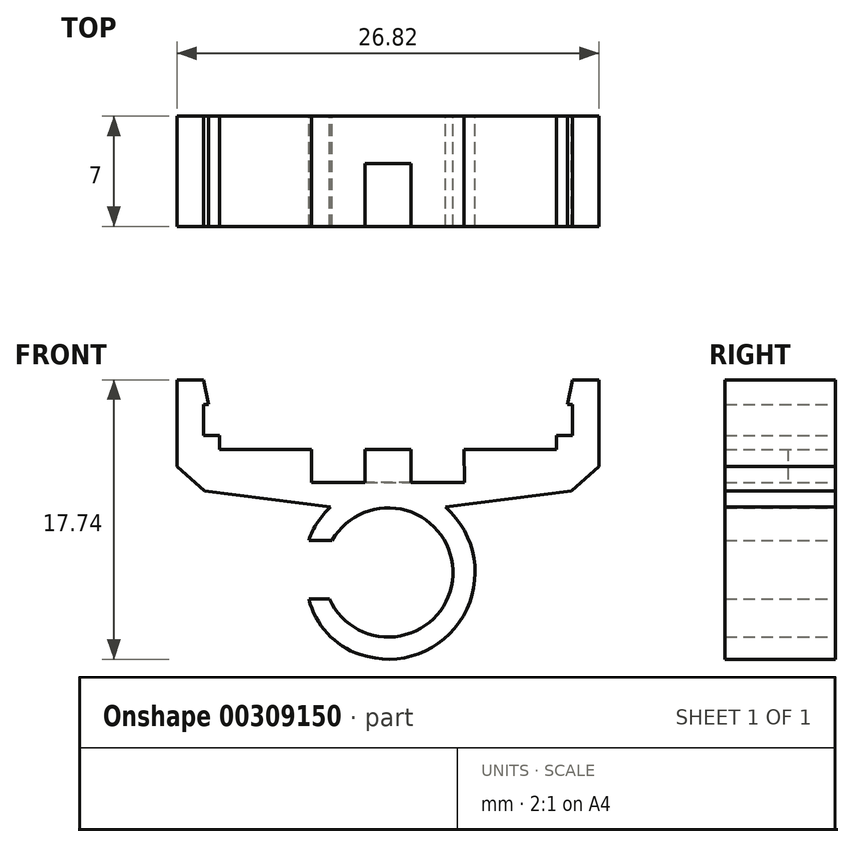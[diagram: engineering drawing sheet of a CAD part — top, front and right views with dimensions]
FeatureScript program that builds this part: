
annotation { "Feature Type Name" : "Feature", "Feature Type Description" : "" }
export const myFeature = defineFeature(function(context is Context, id is Id, definition is map)
    precondition{}
    {
        {
            var Q0;
            Q0=qCreatedBy(makeId("Front.planeOp"),FACE);
            var sketch = newSketch(context, id + "F0", { "sketchPlane" : qUnion([Q0])});
            skLineSegment(sketch, "E0", {"start": v(-2.98, 4.62) * mm, "end": v(-2.98, 4.65) * mm});
            skArc(sketch, "E1.trimOffspring", {"start": v(-1.78, -5.2) * mm, "mid": v(4.78, -2.76) * mm, "end": v(3.65, 4.15) * mm});
            skArc(sketch, "E2", {"start": v(-3.65, 4.15) * mm, "mid": v(-4.48, 3.19) * mm, "end": v(-5.03, 2.04) * mm});
            skArc(sketch, "E3", {"start": v(-5.03, -1.68) * mm, "mid": v(-3.86, -3.86) * mm, "end": v(-1.78, -5.2) * mm});
            skLineSegment(sketch, "E4", {"start": v(11.65, 5.17) * mm, "end": v(13.41, 6.73) * mm});
            skLineSegment(sketch, "E5", {"start": v(11.7, 8.7) * mm, "end": v(11.7, 9.57) * mm});
            skLineSegment(sketch, "E6", {"start": v(11.7, 12.23) * mm, "end": v(13.41, 12.23) * mm});
            skLineSegment(sketch, "E7", {"start": v(13.41, 6.73) * mm, "end": v(13.41, 12.23) * mm});
            skLineSegment(sketch, "E8.MirrorCS", {"start": v(-11.65, 5.17) * mm, "end": v(-13.41, 6.73) * mm});
            skLineSegment(sketch, "E9.MirrorCS", {"start": v(-13.41, 6.73) * mm, "end": v(-13.41, 12.23) * mm});
            skLineSegment(sketch, "E10.MirrorCS", {"start": v(-11.7, 8.7) * mm, "end": v(-11.7, 9.57) * mm});
            skLineSegment(sketch, "E11.MirrorCS", {"start": v(-11.7, 12.23) * mm, "end": v(-13.41, 12.23) * mm});
            skLineSegment(sketch, "E12", {"start": v(3.65, 4.15) * mm, "end": v(11.65, 5.17) * mm});
            skLineSegment(sketch, "E13.MirrorCS", {"start": v(-3.65, 4.15) * mm, "end": v(-11.65, 5.17) * mm});
            skPoint(sketch, "E14.MirrorCS.end.orphan", {"position": v(-11.65, 5.17) * mm});
            skLineSegment(sketch, "E15", {"start": v(-4.86, 5.72) * mm, "end": v(4.86, 5.72) * mm});
            skLineSegment(sketch, "E16", {"start": v(-10.7, 7.82) * mm, "end": v(-4.86, 7.82) * mm});
            skLineSegment(sketch, "E17", {"start": v(4.84, 7.82) * mm, "end": v(10.7, 7.82) * mm});
            skLineSegment(sketch, "E18", {"start": v(-4.86, 5.72) * mm, "end": v(-4.86, 7.82) * mm});
            skLineSegment(sketch, "E19", {"start": v(4.86, 5.72) * mm, "end": v(4.84, 7.82) * mm});
            skLineSegment(sketch, "E20", {"start": v(11.7, 8.7) * mm, "end": v(11.7, 10.66) * mm});
            skLineSegment(sketch, "E21", {"start": v(11.7, 8.7) * mm, "end": v(10.7, 8.7) * mm});
            skLineSegment(sketch, "E22", {"start": v(10.7, 8.7) * mm, "end": v(10.7, 7.82) * mm});
            skPoint(sketch, "E23.orphan", {"position": v(11.7, 7.82) * mm});
            skLineSegment(sketch, "E24.MirrorCS", {"start": v(-10.7, 8.7) * mm, "end": v(-10.7, 7.82) * mm});
            skLineSegment(sketch, "E25.MirrorCS", {"start": v(-11.7, 8.7) * mm, "end": v(-10.7, 8.7) * mm});
            skLineSegment(sketch, "E26.MirrorCS", {"start": v(-11.7, 8.7) * mm, "end": v(-11.7, 10.66) * mm});
            skPoint(sketch, "E27.orphan", {"position": v(-11.7, 9.57) * mm});
            skPoint(sketch, "E28.orphan", {"position": v(-11.7, 7.82) * mm});
            skLineSegment(sketch, "E29", {"start": v(-11.7, 10.66) * mm, "end": v(-11.7, 12.23) * mm});
            skLineSegment(sketch, "E30", {"start": v(11.7, 10.66) * mm, "end": v(11.7, 12.23) * mm});
            skPoint(sketch, "E31.MirrorCS.start.orphan", {"position": v(-11.7, 10.66) * mm});
            skLineSegment(sketch, "E32", {"start": v(-11.7, 10.66) * mm, "end": v(-11.4, 10.66) * mm});
            skLineSegment(sketch, "E33", {"start": v(-11.4, 10.66) * mm, "end": v(-11.7, 12.23) * mm});
            skLineSegment(sketch, "E34", {"start": v(11.7, 10.66) * mm, "end": v(11.4, 10.66) * mm});
            skLineSegment(sketch, "E35", {"start": v(11.4, 10.66) * mm, "end": v(11.7, 12.23) * mm});
            skLineSegment(sketch, "E36", {"start": v(0, 5.72) * mm, "end": v(0, 7.82) * mm, "construction": true});
            skLineSegment(sketch, "E37", {"start": v(0, 7.82) * mm, "end": v(-1.45, 7.82) * mm});
            skLineSegment(sketch, "E38.MirrorCS", {"start": v(0, 7.82) * mm, "end": v(1.45, 7.82) * mm});
            skLineSegment(sketch, "E39", {"start": v(-1.45, 7.82) * mm, "end": v(-1.45, 5.72) * mm});
            skLineSegment(sketch, "E40", {"start": v(1.45, 7.82) * mm, "end": v(1.45, 5.72) * mm});
            skArc(sketch, "E41", {"start": v(-3.73, -1.68) * mm, "mid": v(4.12, -0.2) * mm, "end": v(-3.55, 2.04) * mm});
            skLineSegment(sketch, "E42", {"start": v(-5.03, 2.04) * mm, "end": v(-3.55, 2.04) * mm});
            skLineSegment(sketch, "E43", {"start": v(-5.03, -1.68) * mm, "end": v(-3.73, -1.68) * mm});
            skLineSegment(sketch, "E44", {"start": v(-4.81, -2.36) * mm, "end": v(5, 2.35) * mm, "construction": true});
            skLineSegment(sketch, "E45", {"start": v(-3.05, 2.73) * mm, "end": v(3.11, -2.7) * mm, "construction": true});
            skSolve(sketch);
        }
        {
            var Q0;
            Q0 = qSketchRegion(id + "F0", true);
            extrude(context, id + "F1", {"entities" : qUnion([Q0]), "depth" : 7 * mm});
        }
        {
            var Q0;
            Q0=makeQuery(id+"F1.opExtrude","CAP_FACE",FACE,{"disambiguationData":[OSD([sQuery(id+"F0.wireOp",EDGE,"E1.trimOffspring"),sQuery(id+"F0.wireOp",EDGE,"E2"),sQuery(id+"F0.wireOp",EDGE,"E3"),sQuery(id+"F0.wireOp",EDGE,"znFwvZoN-sigT-Xg2n-eal0-1niIN2wFVg9l"),sQuery(id+"F0.wireOp",EDGE,"9Rdlhenn-cWnR-pCTD-kgNb-PHPd0827WlvZ"),sQuery(id+"F0.wireOp",EDGE,"7K4rQpHj-UDtW-EEUH-9ahp-Sysw3BNcFUdX"),sQuery(id+"F0.wireOp",EDGE,"E4"),sQuery(id+"F0.wireOp",EDGE,"E6"),sQuery(id+"F0.wireOp",EDGE,"E7"),sQuery(id+"F0.wireOp",EDGE,"E8.MirrorCS"),sQuery(id+"F0.wireOp",EDGE,"E9.MirrorCS"),sQuery(id+"F0.wireOp",EDGE,"E11.MirrorCS"),sQuery(id+"F0.wireOp",EDGE,"E12"),sQuery(id+"F0.wireOp",EDGE,"E13.MirrorCS"),sQuery(id+"F0.wireOp",EDGE,"E15"),sQuery(id+"F0.wireOp",EDGE,"E16"),sQuery(id+"F0.wireOp",EDGE,"E17"),sQuery(id+"F0.wireOp",EDGE,"E18"),sQuery(id+"F0.wireOp",EDGE,"E19"),sQuery(id+"F0.wireOp",EDGE,"E20"),sQuery(id+"F0.wireOp",EDGE,"E21"),sQuery(id+"F0.wireOp",EDGE,"E22"),sQuery(id+"F0.wireOp",EDGE,"E24.MirrorCS"),sQuery(id+"F0.wireOp",EDGE,"E25.MirrorCS"),sQuery(id+"F0.wireOp",EDGE,"E26.MirrorCS"),sQuery(id+"F0.wireOp",EDGE,"E32"),sQuery(id+"F0.wireOp",EDGE,"E33"),sQuery(id+"F0.wireOp",EDGE,"E34"),sQuery(id+"F0.wireOp",EDGE,"E35"),sQuery(id+"F0.wireOp",EDGE,"E37"),sQuery(id+"F0.wireOp",EDGE,"E38.MirrorCS"),sQuery(id+"F0.wireOp",EDGE,"E39"),sQuery(id+"F0.wireOp",EDGE,"E40")])],"isStart":true});
            var sketch = newSketch(context, id + "F2", { "sketchPlane" : qUnion([Q0])});
            skLineSegment(sketch, "E46.bottom", {"start": v(-1.45, 7.82) * mm, "end": v(1.45, 7.82) * mm});
            skLineSegment(sketch, "E46.top", {"start": v(-1.45, 5.72) * mm, "end": v(1.45, 5.72) * mm});
            skLineSegment(sketch, "E46.left", {"start": v(-1.45, 7.82) * mm, "end": v(-1.45, 5.72) * mm});
            skLineSegment(sketch, "E46.right", {"start": v(1.45, 7.82) * mm, "end": v(1.45, 5.72) * mm});
            skSolve(sketch);
        }
        {
            var Q0;
            Q0 = qSketchRegion(id + "F2", true);
            extrude(context, id + "F3", {"entities" : qUnion([Q0]), "operationType" : NewBodyOperationType.REMOVE, "oppositeDirection" : true, "depth" : 3 * mm});
        }
    });
